# Revit family: Bath Tub_Hi Macs_CB680
name_source: partatom
category: Plumbing Fixtures
revit_build: Autodesk Revit Architecture 2014 (Build: 20131024_2115(x64)
units: mm (PartAtom-declared; Revit-internal decimal feet)

## types (1)
- Bath Tub_Hi Macs_CB680
    BIMobject category = Sanitary
    Date of publishing = 2014-10-09
    Depth = 471 mm
    Description = Nothing less than the maximum level of hygiene, ergonomics and warmth is good enough for the neonatal ward of any hospital. With ultra-soft corners and contours ergonomically designed specifically for babies, the new HI-MACS® Baby Bath is the perfect product for babies' first baths of their lives.
    Design country = Italy
    Edition number = 1
    Height = 172 mm  [stored 0.564304 ft]
    IFC Classification = Furnishing Element
    Installation instructions = http://himacs.eu
    Manufacturer URL = http://www.himacs.eu
    Manufacturer country = Italy
    Manufacturer name = HI-MACS
    Material Main = Natural Acrylic Stone_Hi Macs CB680_Cream
    Material Secondary = Steel_Hi Macs CB680_Cream
    NBS Reference Code = 35-65-70-94
    NBS Reference Description = Wash Basin Systems
    Nominal height = 172
    Nominal width = 751
    Product SKU = CB680
    Product data url = http://www.himacs.eu
    Product family = Sinks, Baby Baths & Bowls
    Product group = Baby Baths
    QR code = http://himacs.bimobject.com
    Technical description = http://himacs.eu
    UNSPSC Code = 301815
    Uniclass 1.4 Code = L7212
    Uniclass 1.4 Description = Washbasins
    Uniclass 2.0 Code = SS-35-65-70-94
    Uniclass 2.0 Description = Wash Basin Systems
    Weight Net (Kg) = 10,8
    Width = 751 mm  [stored 2.46391 ft]

note: [stored X ft] marks values corroborated as IEEE doubles in the binary element streams (Revit-internal decimal feet)

## geometry (parser evidence)
native form markers: Sweep x5
no freeform markers — native parametric forms only
